FCSTD DOCUMENT  (FreeCAD 0.21R33771 (Git))
Label: jrobot-cnc-assembly
License: All rights reserved
LicenseURL: http://en.wikipedia.org/wiki/All_rights_reserved
objects: App::Link×7, App::DocumentObjectGroup×3, PartDesign::CoordinateSystem×1, App::FeaturePython×1, App::Part×1, Spreadsheet::Sheet×1
note: 1 computed .brp shape members not serialized (recipe doc carries the construction recipe); baked Part::Feature solids carry a one-line shape summary decoded from their .brp
EXTERNAL_REF file=standard-parts.FCStd obj=LCS_Arduino_CNCShield_Origin
EXTERNAL_REF file=standard-parts.FCStd obj=Part039
EXTERNAL_REF file=standard-parts.FCStd obj=LCS_Arduino_CNCShield_MotorDriver0
EXTERNAL_REF file=standard-parts.FCStd obj=LCS_Arduino_StepperDriver_Origin
EXTERNAL_REF file=standard-parts.FCStd obj=Part040
EXTERNAL_REF file=standard-parts.FCStd obj=LCS_Arduino_CNCShield_MotorDriver1
EXTERNAL_REF file=standard-parts.FCStd obj=LCS_Arduino_CNCShield_MotorDriver2
EXTERNAL_REF file=standard-parts.FCStd obj=LCS_HeatSink_15mm_HeatSink
EXTERNAL_REF file=standard-parts.FCStd obj=LCS_HeatSink_15mm_Origin
EXTERNAL_REF file=standard-parts.FCStd obj=Part042

FEATURE [App::DocumentObjectGroup] Parts
FEATURE [PartDesign::CoordinateSystem] LCS_Origin
  AttacherType = Attacher::AttachEngine3D
  MapMode = 2
  Support = -> [X_Axis]
FEATURE [App::DocumentObjectGroup] Constraints
FEATURE [App::FeaturePython] Variables  # WARN: FeaturePython — macro-defined, semantics opaque (R4)
  Type = App::PropertyContainer
FEATURE [App::DocumentObjectGroup] Configurations
FEATURE [App::Link] P_Arduino_CNCShield  label="P_Arduino_CNCShield0"
  AttachedBy = #LCS_Arduino_CNCShield_Origin
  AttachedTo = Parent Assembly#LCS_Origin
  LinkedObject = -> <external standard-parts.FCStd>#Part039
  SolverId = Asm4EE
  expr: Placement = LCS_Origin.Placement * AttachmentOffset * standard_parts#LCS_Arduino_CNCShield_Origin.Placement ^ -1
FEATURE [App::Link] P_Arduino_StepperDriver  label="P_Arduino_StepperDriver_CNC0_X"
  AttachedBy = #LCS_Arduino_StepperDriver_Origin
  AttachedTo = P_Arduino_CNCShield#LCS_Arduino_CNCShield_MotorDriver0
  AttachmentOffset = pos=(0,0,0) rot=(0,0,1;4.71239rad)
  LinkPlacement = pos=(-3,13,7) rot=(0,0,1;4.71239rad)
  LinkedObject = -> <external standard-parts.FCStd>#Part040
  Placement = pos=(-3,13,7) rot=(0,0,1;4.71239rad)
  SolverId = Asm4EE
  expr: Placement = P_Arduino_CNCShield.Placement * standard_parts#LCS_Arduino_CNCShield_MotorDriver0.Placement * AttachmentOffset * standard_parts#LCS_Arduino_StepperDriver_Origin.Placement ^ -1
FEATURE [App::Link] P_Arduino_StepperDriver_2  label="P_Arduino_StepperDriver_CNC0_Y"
  AttachedBy = #LCS_Arduino_StepperDriver_Origin
  AttachedTo = P_Arduino_CNCShield#LCS_Arduino_CNCShield_MotorDriver1
  AttachmentOffset = pos=(0,0,0) rot=(0,0,1;4.71239rad)
  LinkPlacement = pos=(-3,-13,7) rot=(0,0,1;4.71239rad)
  LinkedObject = -> <external standard-parts.FCStd>#Part040
  Placement = pos=(-3,-13,7) rot=(0,0,1;4.71239rad)
  SolverId = Asm4EE
  expr: Placement = P_Arduino_CNCShield.Placement * standard_parts#LCS_Arduino_CNCShield_MotorDriver1.Placement * AttachmentOffset * standard_parts#LCS_Arduino_StepperDriver_Origin.Placement ^ -1
FEATURE [App::Link] P_Arduino_StepperDriver_1  label="P_Arduino_StepperDriver_CNC0_Z"
  AttachedBy = #LCS_Arduino_StepperDriver_Origin
  AttachedTo = P_Arduino_CNCShield#LCS_Arduino_CNCShield_MotorDriver2
  AttachmentOffset = pos=(0,0,0) rot=(0,0,1;4.71239rad)
  LinkPlacement = pos=(22,13,7) rot=(0,0,1;4.71239rad)
  LinkedObject = -> <external standard-parts.FCStd>#Part040
  Placement = pos=(22,13,7) rot=(0,0,1;4.71239rad)
  SolverId = Asm4EE
  expr: Placement = P_Arduino_CNCShield.Placement * standard_parts#LCS_Arduino_CNCShield_MotorDriver2.Placement * AttachmentOffset * standard_parts#LCS_Arduino_StepperDriver_Origin.Placement ^ -1
FEATURE [App::Link] P_HeatSink_15mm  label="P_HeatSink_15mm_X"
  AttachedBy = #LCS_HeatSink_15mm_Origin
  AttachedTo = P_Arduino_StepperDriver#LCS_HeatSink_15mm_HeatSink
  LinkPlacement = pos=(-3,13,11) rot=(0,0,1;4.71239rad)
  LinkedObject = -> <external standard-parts.FCStd>#Part042
  Placement = pos=(-3,13,11) rot=(0,0,1;4.71239rad)
  SolverId = Asm4EE
  expr: Placement = P_Arduino_StepperDriver.Placement * standard_parts#LCS_HeatSink_15mm_HeatSink.Placement * AttachmentOffset * standard_parts#LCS_HeatSink_15mm_Origin.Placement ^ -1
FEATURE [App::Link] P_HeatSink_15mm_2  label="P_HeatSink_15mm_Y"
  AttachedBy = #LCS_HeatSink_15mm_Origin
  AttachedTo = P_Arduino_StepperDriver_2#LCS_HeatSink_15mm_HeatSink
  LinkPlacement = pos=(-3,-13,11) rot=(0,0,1;4.71239rad)
  LinkedObject = -> <external standard-parts.FCStd>#Part042
  Placement = pos=(-3,-13,11) rot=(0,0,1;4.71239rad)
  SolverId = Asm4EE
  expr: Placement = P_Arduino_StepperDriver_2.Placement * standard_parts#LCS_HeatSink_15mm_HeatSink.Placement * AttachmentOffset * standard_parts#LCS_HeatSink_15mm_Origin.Placement ^ -1
FEATURE [App::Link] P_HeatSink_15mm_1  label="P_HeatSink_15mm_Z"
  AttachedBy = #LCS_HeatSink_15mm_Origin
  AttachedTo = P_Arduino_StepperDriver_1#LCS_HeatSink_15mm_HeatSink
  LinkPlacement = pos=(22,13,11) rot=(0,0,1;4.71239rad)
  LinkedObject = -> <external standard-parts.FCStd>#Part042
  Placement = pos=(22,13,11) rot=(0,0,1;4.71239rad)
  SolverId = Asm4EE
  expr: Placement = P_Arduino_StepperDriver_1.Placement * standard_parts#LCS_HeatSink_15mm_HeatSink.Placement * AttachmentOffset * standard_parts#LCS_HeatSink_15mm_Origin.Placement ^ -1
FEATURE [App::Part] Assembly
  AssemblyType = Part::Link
  DrawingName = jrobot-cnc-assembly.FCStd
  Group = -> [LCS_Origin,Constraints,Variables,Configurations,P_Arduino_CNCShield,P_Arduino_StepperDriver,P_Arduino_StepperDriver_2,P_Arduino_StepperDriver_1,P_HeatSink_15mm,P_HeatSink_15mm_2,P_HeatSink_15mm_1]
  Origin = -> Origin
  PartID = jrobot-cnc-assembly
  Type = Assembly
FEATURE [Spreadsheet::Sheet] BOM
  cells = A1='BomKey; B1='DrawingName; C1='DrawingRevision; D1='PartID; E1='PartDescription; F1='FileName; G1='FastenerDiameter; H1='FastenerLength; I1='FastenerType; J1='Qty.; A2='jrobot_cnc_assembly#Assembly; B2='jrobot-cnc-assembly.FCStd; D2='jrobot-cnc-assembly; G2='-; H2='-; I2='-; J2=1; A3='standard_parts#Part039; B3='standard-parts.FCStd; D3='standard-parts; E3='B_Arduino_CNCShield; G3='-; H3='-; I3='-; J3=1; A4='standard_parts#Part040; B4='standard-parts.FCStd; D4='standard-parts; E4='B_Arduino_StepperDriver; G4='-; H4='-; I4='-; J4=3; A5='standard_parts#Part042; B5='standard-parts.FCStd; D5='standard-parts; E5='B_HeatSink_15mm; G5='-; H5='-; I5='-; J5=3

RESOLVED EXTERNAL PARTS (link-assembly join: the EXTERNAL_REF files above that resolve inside this repo's crawl, each included once):
---- part standard-parts.FCStd = doc fcstd_9b47ef122aeb (208734 chars; too large to inline — full recipe in that document) ----
